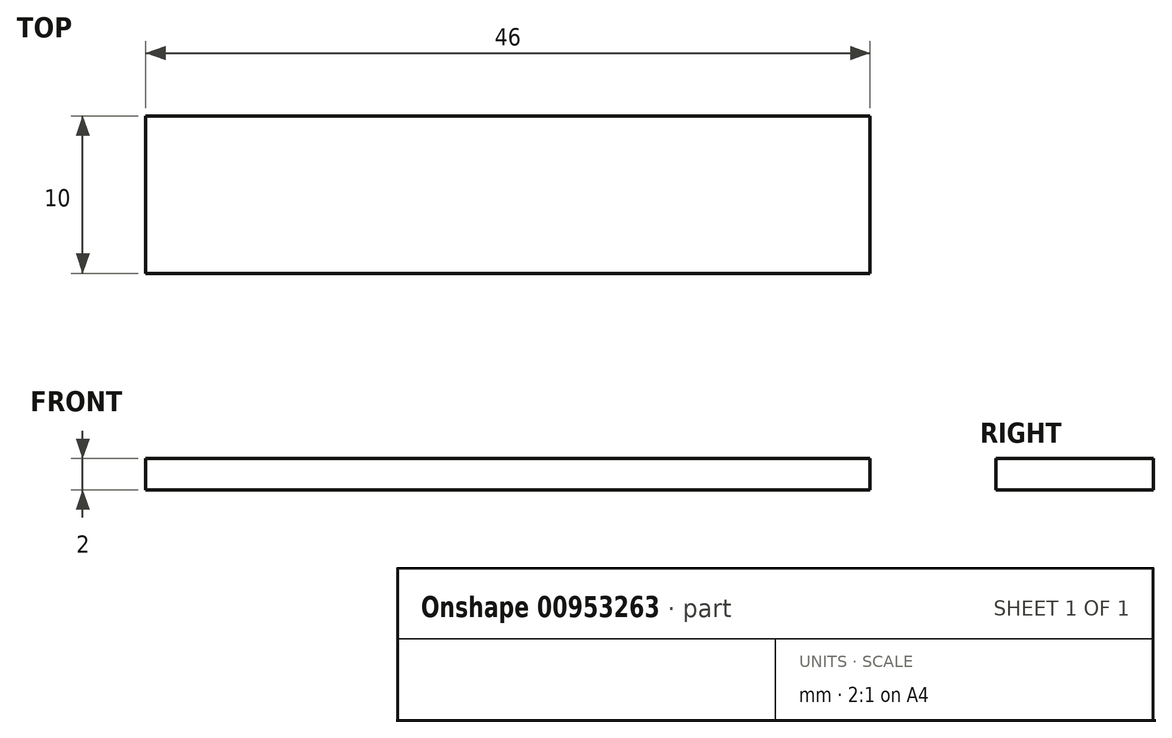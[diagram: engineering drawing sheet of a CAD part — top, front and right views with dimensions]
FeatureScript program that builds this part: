
annotation { "Feature Type Name" : "Feature", "Feature Type Description" : "" }
export const myFeature = defineFeature(function(context is Context, id is Id, definition is map)
    precondition{}
    {
        {
            var Q0;
            Q0=qCreatedBy(makeId("Top.planeOp"),FACE);
            var sketch = newSketch(context, id + "F0", { "sketchPlane" : qUnion([Q0])});
            skLineSegment(sketch, "E0.bottom", {"start": v(-10.53, -12.68) * mm, "end": v(35.47, -12.68) * mm});
            skLineSegment(sketch, "E0.top", {"start": v(-10.53, -2.68) * mm, "end": v(35.47, -2.68) * mm});
            skLineSegment(sketch, "E0.left", {"start": v(-10.53, -12.68) * mm, "end": v(-10.53, -2.68) * mm});
            skLineSegment(sketch, "E0.right", {"start": v(35.47, -12.68) * mm, "end": v(35.47, -2.68) * mm});
            skSolve(sketch);
        }
        {
            var Q0;
            Q0=makeQuery(id+"F0.imprint","IMPRINT",FACE,{"disambiguationData":[TD([[makeQuery(id+"F0.imprint","IMPRINT",EDGE,{"derivedFrom":sQuery(id+"F0.wireOp",EDGE,"E0.bottom")}),1.0]])]});
            extrude(context, id + "F1", {"entities" : qUnion([Q0]), "depth" : 2 * mm, "offsetDistance" : 25.4 * mm});
        }
    });
